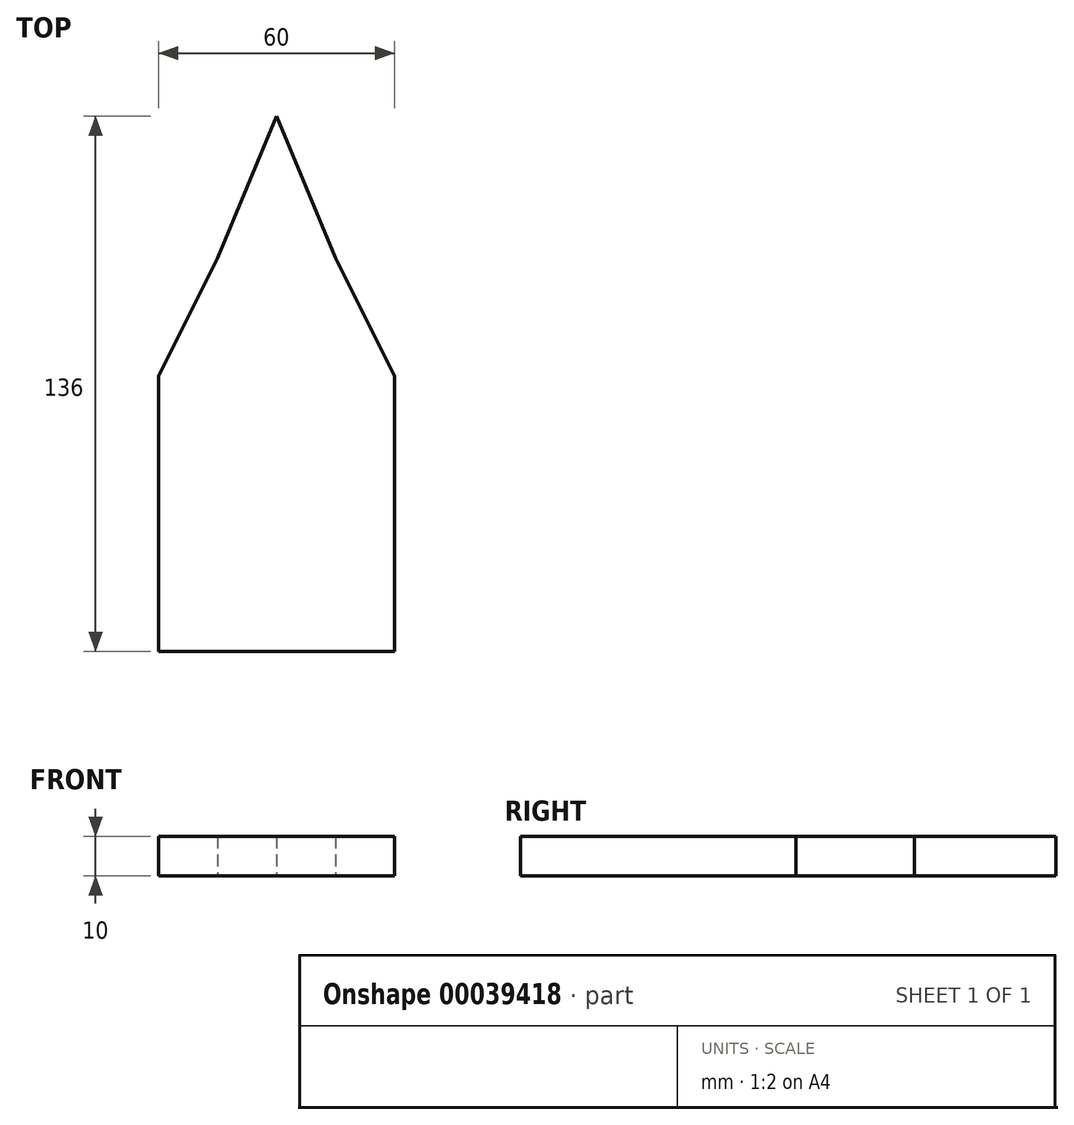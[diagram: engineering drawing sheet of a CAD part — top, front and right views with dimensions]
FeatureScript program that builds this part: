
annotation { "Feature Type Name" : "Feature", "Feature Type Description" : "" }
export const myFeature = defineFeature(function(context is Context, id is Id, definition is map)
    precondition{}
    {
        {
            var Q0;
            Q0=qCreatedBy(makeId("Top.planeOp"),FACE);
            var sketch = newSketch(context, id + "F0", { "sketchPlane" : qUnion([Q0])});
            skLineSegment(sketch, "E0.bottom", {"start": v(-40.7, 17.13) * mm, "end": v(19.3, 17.13) * mm});
            skLineSegment(sketch, "E0.top", {"start": v(-40.7, -52.87) * mm, "end": v(19.3, -52.87) * mm});
            skLineSegment(sketch, "E0.left", {"start": v(-40.7, 17.13) * mm, "end": v(-40.7, -52.87) * mm});
            skLineSegment(sketch, "E0.right", {"start": v(19.3, 17.13) * mm, "end": v(19.3, -52.87) * mm});
            skLineSegment(sketch, "E1.top", {"start": v(-25.7, 47.13) * mm, "end": v(4.3, 47.13) * mm});
            skLineSegment(sketch, "E2", {"start": v(-40.7, 17.13) * mm, "end": v(-25.7, 47.13) * mm});
            skLineSegment(sketch, "E3", {"start": v(19.3, 17.13) * mm, "end": v(4.3, 47.13) * mm});
            skLineSegment(sketch, "E4", {"start": v(-25.7, 47.13) * mm, "end": v(-10.7, 83.13) * mm});
            skLineSegment(sketch, "E5", {"start": v(-10.7, 83.13) * mm, "end": v(4.3, 47.13) * mm});
            skLineSegment(sketch, "E6", {"start": v(-10.7, 47.13) * mm, "end": v(-10.7, 17.13) * mm, "construction": true});
            skLineSegment(sketch, "E7", {"start": v(-10.7, 83.13) * mm, "end": v(-10.7, 47.13) * mm, "construction": true});
            skSolve(sketch);
        }
        {
            var Q0;
            Q0=makeQuery(id+"F0.imprint","IMPRINT",FACE,{"disambiguationData":[TD([[makeQuery(id+"F0.imprint","IMPRINT",EDGE,{"derivedFrom":sQuery(id+"F0.wireOp",EDGE,"E1.top")}),1.0]])]});
            var Q1;
            Q1=makeQuery(id+"F0.imprint","IMPRINT",FACE,{"disambiguationData":[TD([[makeQuery(id+"F0.imprint","IMPRINT",EDGE,{"derivedFrom":sQuery(id+"F0.wireOp",EDGE,"E0.bottom")}),1.0]])]});
            var Q2;
            Q2=makeQuery(id+"F0.imprint","IMPRINT",FACE,{"disambiguationData":[TD([[makeQuery(id+"F0.imprint","IMPRINT",EDGE,{"derivedFrom":sQuery(id+"F0.wireOp",EDGE,"E0.top")}),1.0]])]});
            extrude(context, id + "F1", {"entities" : qUnion([Q0, Q1, Q2]), "depth" : 10 * mm});
        }
    });
